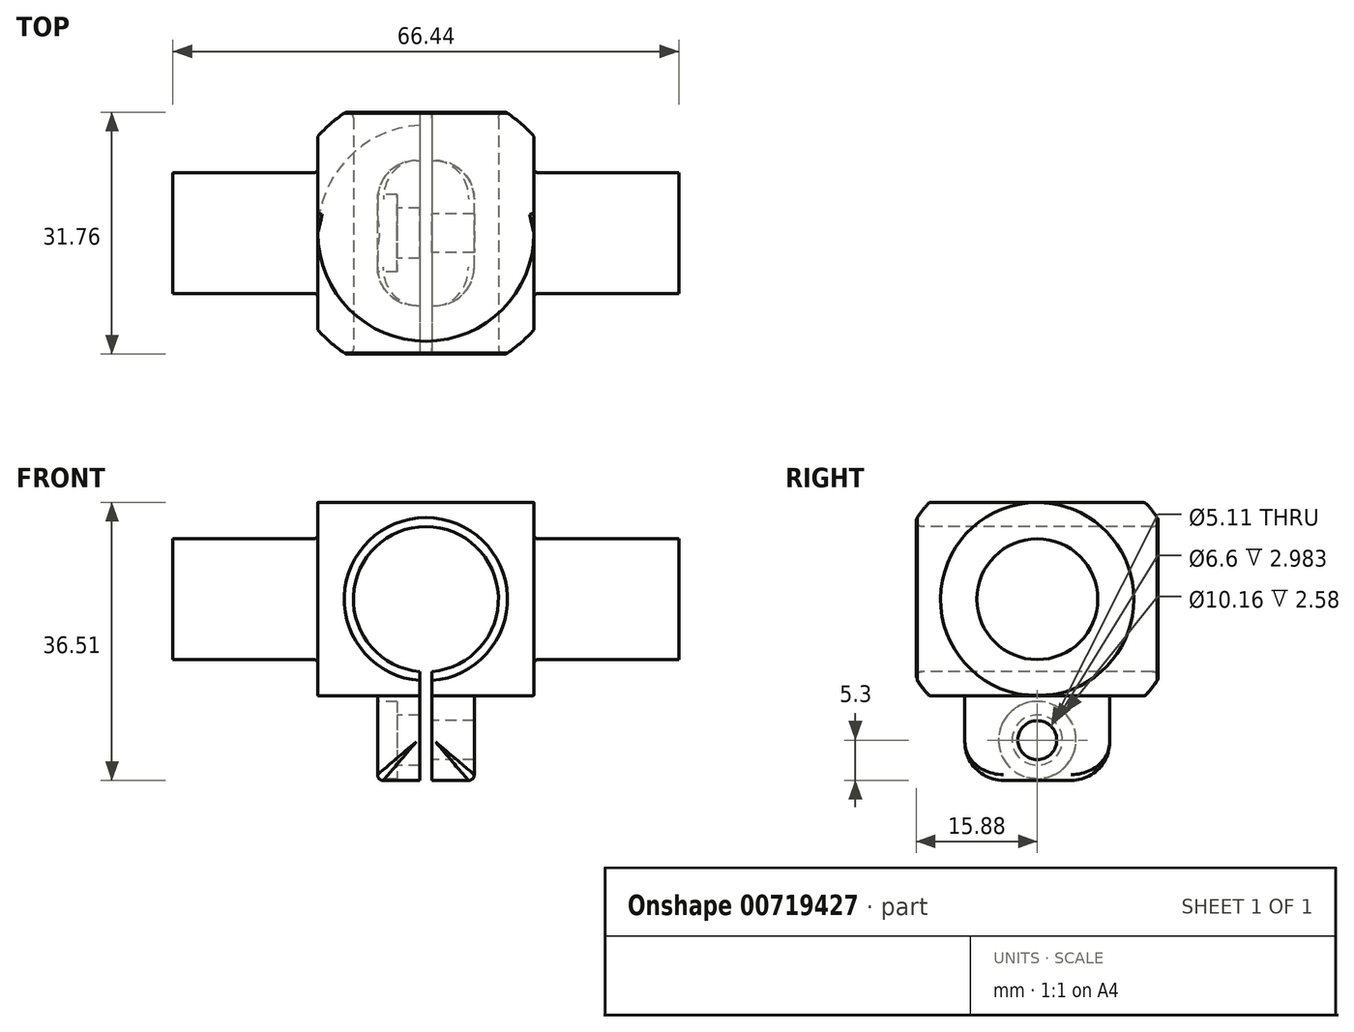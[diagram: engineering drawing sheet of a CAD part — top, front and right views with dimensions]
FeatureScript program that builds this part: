
annotation { "Feature Type Name" : "Feature", "Feature Type Description" : "" }
export const myFeature = defineFeature(function(context is Context, id is Id, definition is map)
    precondition{}
    {
        {
            var Q0;
            Q0=qCreatedBy(makeId("Front.planeOp"),FACE);
            var sketch = newSketch(context, id + "F0", { "sketchPlane" : qUnion([Q0])});
            skLineSegment(sketch, "E0", {"start": v(0, 12.7) * mm, "end": v(14.2, 12.7) * mm});
            skLineSegment(sketch, "E1.MirrorCS", {"start": v(0, -12.7) * mm, "end": v(14.2, -12.7) * mm});
            skArc(sketch, "E2.trimOffspring", {"start": v(14.2, -12.7) * mm, "mid": v(19.05, 0) * mm, "end": v(14.2, 12.7) * mm});
            skLineSegment(sketch, "E3", {"start": v(0, 12.7) * mm, "end": v(0, -12.7) * mm});
            skSolve(sketch);
        }
        {
            var Q0;
            Q0 = qSketchRegion(id + "F0", true);
            var Q1;
            Q1=sQuery(id+"F0.wireOp",EDGE,"E3");
            revolve(context, id + "F1", {"surfaceOperationType" : NewSurfaceOperationType.NEW, "entities" : qUnion([Q0]), "axis" : qUnion([Q1]), "revolveType" : RevolveType.FULL});
        }
        {
            var Q0;
            Q0=qCreatedBy(makeId("Right.planeOp"),FACE);
            var sketch = newSketch(context, id + "F2", { "sketchPlane" : qUnion([Q0])});
            skCircle(sketch, "E4", {"center": v(0, 0) * mm, "radius": 7.94 * mm});
            skSolve(sketch);
        }
        {
            var Q0;
            Q0 = qSketchRegion(id + "F2", true);
            extrude(context, id + "F3", {"entities" : qUnion([Q0]), "depth" : 33.22 * mm, "offsetDistance" : 25.4 * mm});
        }
        {
            var Q0;
            Q0=makeQuery(id+"F3.opExtrude","SWEPT_BODY",BODY,{"disambiguationData":[OSD([sQuery(id+"F2.wireOp",EDGE,"E4")])]});
            var Q1;
            Q1=qCreatedBy(makeId("Right.planeOp"),FACE);
            mirror(context, id + "F4", {"operationType" : NewBodyOperationType.ADD, "entities" : qUnion([Q0]), "mirrorPlane" : qUnion([Q1])});
        }
        {
            var Q0;
            Q0=qCreatedBy(makeId("Front.planeOp"),FACE);
            var sketch = newSketch(context, id + "F5", { "sketchPlane" : qUnion([Q0])});
            skCircle(sketch, "E5", {"center": v(0, 0) * mm, "radius": 9.53 * mm});
            skSolve(sketch);
        }
        {
            var Q0;
            Q0 = qSketchRegion(id + "F5", true);
            extrude(context, id + "F6", {"entities" : qUnion([Q0]), "operationType" : NewBodyOperationType.REMOVE, "endBound" : BoundingType.THROUGH_ALL, "oppositeDirection" : true, "depth" : 25.4 * mm, "offsetDistance" : 25.4 * mm, "hasSecondDirection" : true, "secondDirectionBound" : BoundingType.THROUGH_ALL, "secondDirectionOppositeDirection" : false, "secondDirectionDepth" : 25.4 * mm});
        }
        {
            var Q0;
            Q0=qCreatedBy(makeId("Front.planeOp"),FACE);
            var sketch = newSketch(context, id + "F7", { "sketchPlane" : qUnion([Q0])});
            skLineSegment(sketch, "E6", {"start": v(14.2, 12.7) * mm, "end": v(14.2, 7.94) * mm});
            skLineSegment(sketch, "E7", {"start": v(14.2, 7.94) * mm, "end": v(17.32, 7.94) * mm});
            skArc(sketch, "E8", {"start": v(17.32, 7.94) * mm, "mid": v(15.94, 10.44) * mm, "end": v(14.2, 12.7) * mm});
            skArc(sketch, "E9.MirrorCS", {"start": v(-17.32, 7.94) * mm, "mid": v(-15.94, 10.44) * mm, "end": v(-14.2, 12.7) * mm});
            skLineSegment(sketch, "E10.MirrorCS", {"start": v(-14.2, 12.7) * mm, "end": v(-14.2, 7.94) * mm});
            skLineSegment(sketch, "E11.MirrorCS", {"start": v(-14.2, 7.94) * mm, "end": v(-17.32, 7.94) * mm});
            skSolve(sketch);
        }
        {
            var Q0;
            Q0 = qSketchRegion(id + "F7", true);
            var Q1;
            {var subQ0=makeQuery(id+"F3.opExtrude","SWEPT_FACE",FACE,{"disambiguationData":[OSD([sQuery(id+"F2.wireOp",EDGE,"E4")])]});Q1=makeQuery(id+"F4.boolean.opBoolean","MERGE",FACE,{"disambiguationData":[OD(0.0)],"derivedFrom":[subQ0,makeQuery(id+"F4.opPattern","COPY",FACE,{"derivedFrom":subQ0,"instanceName":"1"})]});}
            revolve(context, id + "F8", {"operationType" : NewBodyOperationType.REMOVE, "surfaceOperationType" : NewSurfaceOperationType.NEW, "entities" : qUnion([Q0]), "axis" : qUnion([Q1]), "revolveType" : RevolveType.FULL, "oppositeDirection" : true});
        }
        {
            var Q0;
            Q0=qCreatedBy(makeId("Front.planeOp"),FACE);
            var sketch = newSketch(context, id + "F9", { "sketchPlane" : qUnion([Q0])});
            skLineSegment(sketch, "E12.bottom", {"start": v(-6.35, -23.81) * mm, "end": v(6.35, -23.81) * mm});
            skLineSegment(sketch, "E12.top", {"start": v(-6.35, -12.7) * mm, "end": v(6.35, -12.7) * mm});
            skLineSegment(sketch, "E12.left", {"start": v(-6.35, -23.81) * mm, "end": v(-6.35, -12.7) * mm});
            skLineSegment(sketch, "E12.right", {"start": v(6.35, -23.81) * mm, "end": v(6.35, -12.7) * mm});
            skSolve(sketch);
        }
        {
            var Q0;
            Q0 = qSketchRegion(id + "F9", true);
            extrude(context, id + "F10", {"entities" : qUnion([Q0]), "operationType" : NewBodyOperationType.ADD, "depth" : 19.05 * mm, "offsetDistance" : 25.4 * mm, "symmetric" : true});
        }
        {
            var Q0;
            Q0=makeQuery(id+"F10.opExtrude","CAP_EDGE",EDGE,{"disambiguationData":[OSD([sQuery(id+"F9.wireOp",EDGE,"E12.left")])],"isStart":false});
            var Q1;
            Q1=makeQuery(id+"F10.opExtrude","CAP_EDGE",EDGE,{"disambiguationData":[OSD([sQuery(id+"F9.wireOp",EDGE,"E12.right")])],"isStart":false});
            var Q2;
            Q2=makeQuery(id+"F10.opExtrude","CAP_EDGE",EDGE,{"disambiguationData":[OSD([sQuery(id+"F9.wireOp",EDGE,"E12.right")])],"isStart":true});
            var Q3;
            Q3=makeQuery(id+"F10.opExtrude","CAP_EDGE",EDGE,{"disambiguationData":[OSD([sQuery(id+"F9.wireOp",EDGE,"E12.left")])],"isStart":true});
            var Q4;
            Q4=makeQuery(id+"F10.opExtrude","CAP_EDGE",EDGE,{"disambiguationData":[OSD([sQuery(id+"F9.wireOp",EDGE,"E12.bottom")])],"isStart":false});
            var Q5;
            Q5=makeQuery(id+"F10.opExtrude","CAP_EDGE",EDGE,{"disambiguationData":[OSD([sQuery(id+"F9.wireOp",EDGE,"E12.bottom")])],"isStart":true});
            fillet(context, id + "F11", {"entities" : qUnion([Q0, Q1, Q2, Q3, Q4, Q5]), "tangentPropagation" : true, "radius" : 5.08 * mm, "defaultsChanged" : false, "vertexSettings" : [], "allowEdgeOverflow" : false});
        }
        {
            var Q0;
            Q0=makeQuery(id+"F10.opExtrude","SWEPT_EDGE",EDGE,{"disambiguationData":[OSD([sQuery(id+"F9.wireOp",EDGE,"E12.top"),sQuery(id+"F9.wireOp",EDGE,"E12.left")])]});
            var Q1;
            Q1=makeQuery(id+"F8.boolean.opBoolean","COPY",EDGE,{"derivedFrom":makeQuery(id+"F8.opRevolve","SWEPT_EDGE",EDGE,{"disambiguationData":[OSD([sQuery(id+"F7.wireOp",EDGE,"E10.MirrorCS"),sQuery(id+"F7.wireOp",EDGE,"E11.MirrorCS")])]})});
            var Q2;
            Q2=makeQuery(id+"F8.boolean.opBoolean","COPY",EDGE,{"derivedFrom":makeQuery(id+"F8.opRevolve","SWEPT_EDGE",EDGE,{"disambiguationData":[OSD([sQuery(id+"F7.wireOp",EDGE,"E6"),sQuery(id+"F7.wireOp",EDGE,"E7")])]})});
            fillet(context, id + "F12", {"entities" : qUnion([Q0, Q1, Q2]), "tangentPropagation" : true, "radius" : 0.5 * mm, "defaultsChanged" : false, "vertexSettings" : [], "allowEdgeOverflow" : false});
        }
        {
            var Q0;
            Q0=makeQuery(id+"F10.opExtrude","SWEPT_FACE",FACE,{"disambiguationData":[OSD([sQuery(id+"F9.wireOp",EDGE,"E12.left")])]});
            var sketch = newSketch(context, id + "F13", { "sketchPlane" : qUnion([Q0])});
            skLineSegment(sketch, "E13", {"start": v(-4.44, -18.51) * mm, "end": v(4.44, -18.51) * mm, "construction": true});
            skPoint(sketch, "E14", {"position": v(0, -18.51) * mm});
            skSolve(sketch);
        }
        {
            var Q0;
            Q0=sQuery(id+"F13.wireOp",VERTEX,"E14");
            var Q1;
            Q1=makeQuery(id+"F1.opRevolve","SWEPT_BODY",BODY,{"disambiguationData":[OSD([sQuery(id+"F0.wireOp",EDGE,"E0"),sQuery(id+"F0.wireOp",EDGE,"E1.MirrorCS"),sQuery(id+"F0.wireOp",EDGE,"E2.trimOffspring"),sQuery(id+"F0.wireOp",EDGE,"E3")])]});
            hole(context, id + "F14", {"style" : HoleStyle.SIMPLE, "endStyle" : HoleEndStyle.THROUGH, "standardTappedOrClearance" : lookupTablePath({ "standard" : "ANSI", "engagement" : "75%", "pitch" : "20 tpi", "size" : "1/4", "type" : "Tapped" }), "standardBlindInLast" : lookupTablePath({ "standard" : "ANSI", "fit" : "Free", "engagement" : "75%", "pitch" : "20 tpi", "size" : "1/4", "type" : "Clearance & tapped" }), "holeDiameter" : 5.1 * mm, "majorDiameter" : 6.35 * mm, "showTappedDepth" : true, "isTappedThrough" : true, "tappedDepth" : 12.7 * mm, "tapClearance" : 3, "locations" : qUnion([Q0]), "scope" : qUnion([Q1])});
        }
        {
            var Q0;
            Q0=qCreatedBy(makeId("Front.planeOp"),FACE);
            var sketch = newSketch(context, id + "F15", { "sketchPlane" : qUnion([Q0])});
            skLineSegment(sketch, "E15.bottom", {"start": v(-0.79, 0) * mm, "end": v(0.79, 0) * mm});
            skLineSegment(sketch, "E15.top", {"start": v(-0.79, -23.81) * mm, "end": v(0.79, -23.81) * mm});
            skLineSegment(sketch, "E15.left", {"start": v(-0.79, 0) * mm, "end": v(-0.79, -23.81) * mm});
            skLineSegment(sketch, "E15.right", {"start": v(0.79, 0) * mm, "end": v(0.79, -23.81) * mm});
            skSolve(sketch);
        }
        {
            var Q0;
            Q0 = qSketchRegion(id + "F15", true);
            extrude(context, id + "F16", {"entities" : qUnion([Q0]), "operationType" : NewBodyOperationType.REMOVE, "oppositeDirection" : true, "depth" : 38.1 * mm, "offsetDistance" : 25.4 * mm, "symmetric" : true});
        }
        {
            var Q0;
            Q0=sQuery(id+"F13.wireOp",VERTEX,"E14");
            var Q1;
            Q1=makeQuery(id+"F1.opRevolve","SWEPT_BODY",BODY,{"disambiguationData":[OSD([sQuery(id+"F0.wireOp",EDGE,"E0"),sQuery(id+"F0.wireOp",EDGE,"E1.MirrorCS"),sQuery(id+"F0.wireOp",EDGE,"E2.trimOffspring"),sQuery(id+"F0.wireOp",EDGE,"E3")])]});
            hole(context, id + "F17", {"style" : HoleStyle.C_BORE, "endStyle" : HoleEndStyle.BLIND, "holeDiameter" : 6.6 * mm, "cBoreDiameter" : 10.16 * mm, "cBoreDepth" : 2.54 * mm, "majorDiameter" : 6.35 * mm, "holeDepth" : 6.35 * mm, "isTappedThrough" : true, "tappedDepth" : 12.7 * mm, "tapClearance" : 3, "locations" : qUnion([Q0]), "scope" : qUnion([Q1])});
        }
        {
            var Q0;
            Q0=makeQuery(id+"F11.opFillet","BLEND_EDGE",EDGE,{"blendedFrom":[makeQuery(id+"F10.opExtrude","CAP_EDGE",EDGE,{"disambiguationData":[OSD([sQuery(id+"F9.wireOp",EDGE,"E12.bottom")])],"isStart":false}),makeQuery(id+"F10.opExtrude","CAP_EDGE",EDGE,{"disambiguationData":[OSD([sQuery(id+"F9.wireOp",EDGE,"E12.left")])],"isStart":false})],"blendedInto":[]});
            var Q1;
            Q1=makeQuery(id+"F11.opFillet","BLEND_EDGE",EDGE,{"blendedFrom":[makeQuery(id+"F10.opExtrude","CAP_EDGE",EDGE,{"disambiguationData":[OSD([sQuery(id+"F9.wireOp",EDGE,"E12.bottom")])],"isStart":false}),makeQuery(id+"F10.opExtrude","CAP_EDGE",EDGE,{"disambiguationData":[OSD([sQuery(id+"F9.wireOp",EDGE,"E12.right")])],"isStart":false})],"blendedInto":[]});
            var Q2;
            Q2=makeQuery(id+"F6.boolean.opBoolean","INTERSECT",EDGE,{"disambiguationData":[OD(1.0)],"derivedFrom":[makeQuery(id+"F1.opRevolve","SWEPT_FACE",FACE,{"disambiguationData":[OSD([sQuery(id+"F0.wireOp",EDGE,"E2.trimOffspring")])]}),makeQuery(id+"F6.opExtrude","SWEPT_FACE",FACE,{"disambiguationData":[OSD([sQuery(id+"F5.wireOp",EDGE,"E5")])]})]});
            var Q3;
            Q3=makeQuery(id+"F6.boolean.opBoolean","INTERSECT",EDGE,{"disambiguationData":[OD(0.0)],"derivedFrom":[makeQuery(id+"F1.opRevolve","SWEPT_FACE",FACE,{"disambiguationData":[OSD([sQuery(id+"F0.wireOp",EDGE,"E2.trimOffspring")])]}),makeQuery(id+"F6.opExtrude","SWEPT_FACE",FACE,{"disambiguationData":[OSD([sQuery(id+"F5.wireOp",EDGE,"E5")])]})]});
            var Q4;
            Q4=makeQuery(id+"F8.boolean.opBoolean","SPLIT",EDGE,{"disambiguationData":[OD(1.0)],"derivedFrom":makeQuery(id+"F1.opRevolve","SWEPT_EDGE",EDGE,{"disambiguationData":[OSD([sQuery(id+"F0.wireOp",EDGE,"E0"),sQuery(id+"F0.wireOp",EDGE,"E2.trimOffspring")])]})});
            var Q5;
            {var subQ0=sQuery(id+"F0.wireOp",EDGE,"E1.MirrorCS");var subQ1=sQuery(id+"F0.wireOp",EDGE,"E2.trimOffspring");Q5=makeQuery(id+"F16.boolean.opBoolean","SPLIT",EDGE,{"disambiguationData":[TD([makeQuery(id+"F8.boolean.opBoolean","COPY",FACE,{"derivedFrom":makeQuery(id+"F8.opRevolve","SWEPT_FACE",FACE,{"disambiguationData":[OSD([sQuery(id+"F7.wireOp",EDGE,"E6")])]})})])],"derivedFrom":makeQuery(id+"F8.boolean.opBoolean","SPLIT",EDGE,{"disambiguationData":[OD(1.0)],"derivedFrom":makeQuery(id+"F1.opRevolve","SWEPT_EDGE",EDGE,{"disambiguationData":[OSD([subQ0,subQ1])]})})});}
            fillet(context, id + "F18", {"entities" : qUnion([Q0, Q1, Q2, Q3, Q4, Q5]), "tangentPropagation" : true, "radius" : 0.76 * mm, "defaultsChanged" : false, "vertexSettings" : [], "allowEdgeOverflow" : false});
        }
    });
